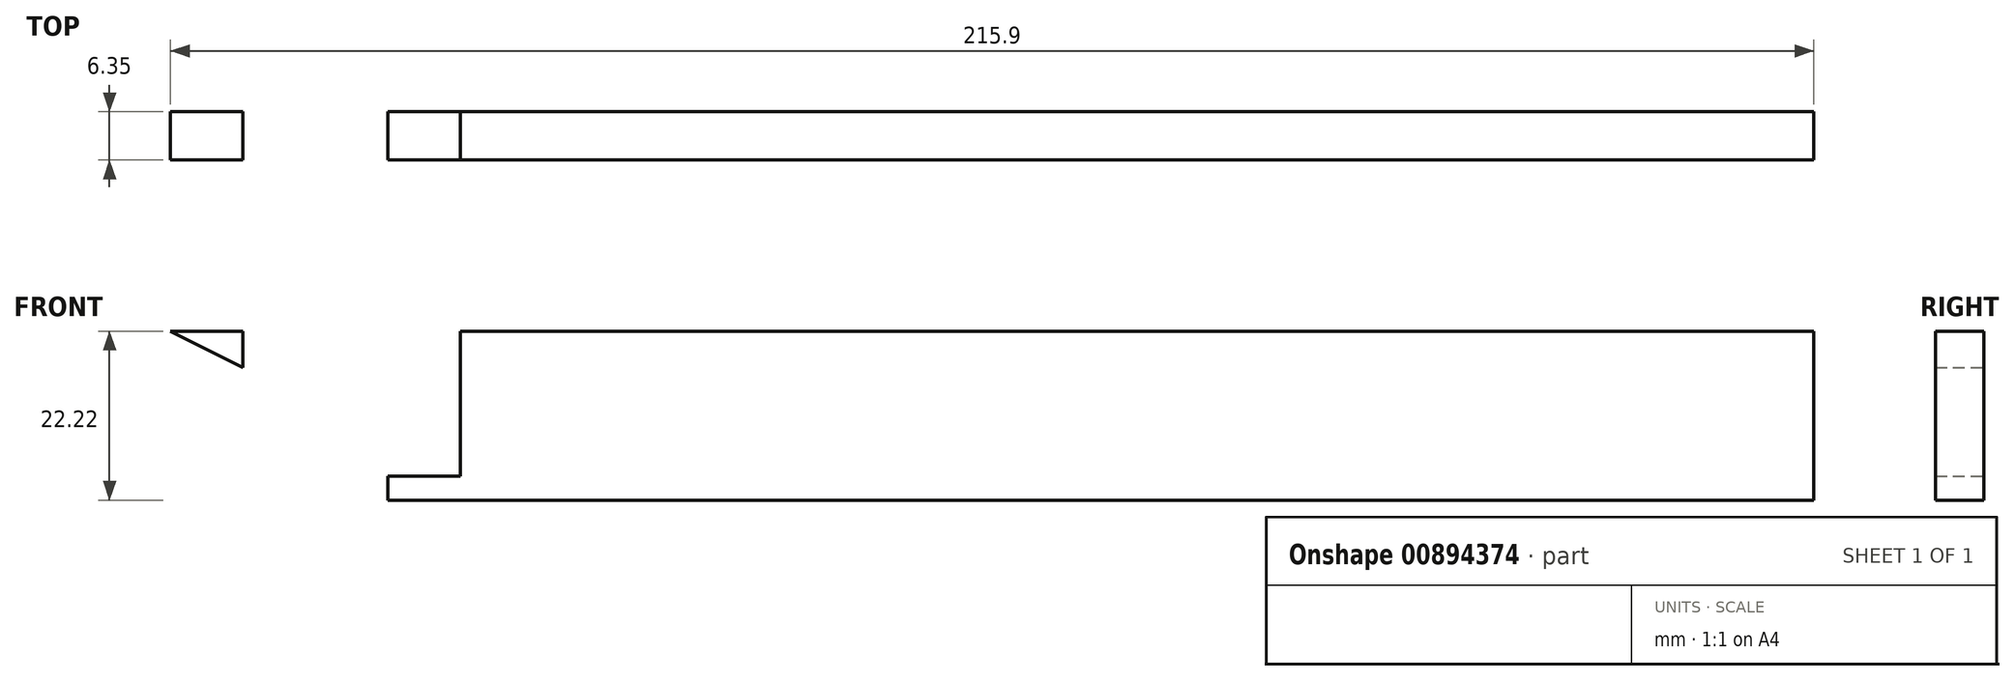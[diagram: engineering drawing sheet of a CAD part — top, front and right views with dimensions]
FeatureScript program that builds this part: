
annotation { "Feature Type Name" : "Feature", "Feature Type Description" : "" }
export const myFeature = defineFeature(function(context is Context, id is Id, definition is map)
    precondition{}
    {
        {
            var Q0;
            Q0=qCreatedBy(makeId("Front.planeOp"),FACE);
            var sketch = newSketch(context, id + "F0", { "sketchPlane" : qUnion([Q0])});
            skLineSegment(sketch, "E0.bottom", {"start": v(15.1, 18.32) * mm, "end": v(192.9, 18.32) * mm});
            skLineSegment(sketch, "E0.top", {"start": v(15.1, 40.54) * mm, "end": v(192.9, 40.54) * mm});
            skLineSegment(sketch, "E0.left", {"start": v(15.1, 18.32) * mm, "end": v(15.1, 40.54) * mm});
            skLineSegment(sketch, "E0.right", {"start": v(192.9, 18.32) * mm, "end": v(192.9, 40.54) * mm});
            skLineSegment(sketch, "E1.bottom", {"start": v(15.1, 18.32) * mm, "end": v(-23, 18.32) * mm});
            skLineSegment(sketch, "E1.top", {"start": v(15.1, 40.54) * mm, "end": v(-23, 40.54) * mm});
            skLineSegment(sketch, "E2.left", {"start": v(-23, 18.32) * mm, "end": v(-23, 15.4) * mm});
            skLineSegment(sketch, "E2.right", {"start": v(-188.1, 18.32) * mm, "end": v(-188.1, -42.13) * mm});
            skArc(sketch, "E3", {"start": v(-23, 18.32) * mm, "mid": v(-36.7, 0.58) * mm, "end": v(-44.36, -20.47) * mm});
            skArc(sketch, "E4", {"start": v(-70.9, 0.58) * mm, "mid": v(-60.95, -14.13) * mm, "end": v(-44.36, -20.47) * mm});
            skPoint(sketch, "E4.startSnap0", {"position": v(-36.7, 0.58) * mm});
            skArc(sketch, "E5", {"start": v(-23, 40.54) * mm, "mid": v(-33.87, 38.07) * mm, "end": v(-42.6, 31.15) * mm});
            skArc(sketch, "E6", {"start": v(-188.1, -42.13) * mm, "mid": v(-127.75, -25.58) * mm, "end": v(-70.9, 0.58) * mm});
            skArc(sketch, "E7", {"start": v(-129.8, 24.44) * mm, "mid": v(-159.01, 21.95) * mm, "end": v(-188.1, 18.32) * mm});
            skArc(sketch, "E8.0", {"start": v(-83.69, 13.36) * mm, "mid": v(-129.64, 11.73) * mm, "end": v(-175.4, 7.24) * mm});
            skArc(sketch, "E8.1", {"start": v(-82.7, 8.57) * mm, "mid": v(-83.01, 11) * mm, "end": v(-83.69, 13.36) * mm});
            skArc(sketch, "E8.2", {"start": v(-175.4, -26.5) * mm, "mid": v(-127.88, -12.07) * mm, "end": v(-82.7, 8.57) * mm});
            skLineSegment(sketch, "E8.3", {"start": v(-175.4, 7.24) * mm, "end": v(-175.4, -26.5) * mm});
            skPoint(sketch, "E9", {"position": v(5.57, 21.5) * mm});
            skLineSegment(sketch, "E10", {"start": v(5.57, 21.5) * mm, "end": v(5.57, 18.32) * mm});
            skLineSegment(sketch, "E11", {"start": v(5.57, 21.5) * mm, "end": v(15.1, 21.5) * mm});
            skLineSegment(sketch, "E12", {"start": v(-23, 40.54) * mm, "end": v(-14.68, 40.54) * mm});
            skLineSegment(sketch, "E13", {"start": v(-23, 40.54) * mm, "end": v(-13.48, 40.54) * mm});
            skLineSegment(sketch, "E14", {"start": v(-13.48, 40.54) * mm, "end": v(-13.48, 35.78) * mm});
            skLineSegment(sketch, "E15", {"start": v(-13.48, 35.78) * mm, "end": v(-23, 40.54) * mm});
            skFitSpline(sketch, "E16", {"points": [v(-42.6, 31.15) * mm, v(-56.97, 17.81) * mm, v(-88.1, 26.02) * mm], "startDerivative": vector(-27.78, -40.13) * mm, "endDerivative": vector(-61.83, 26.33) * mm});
            skFitSpline(sketch, "E17", {"points": [v(-72.62, 19.8) * mm, v(-98.6, 25.84) * mm, v(-129.8, 24.44) * mm], "startDerivative": vector(-52.72, 15.41) * mm, "endDerivative": vector(-61.46, -7.14) * mm});
            skSolve(sketch);
        }
        {
            var Q0;
            {var subQ3=sQuery(id+"F0.wireOp",EDGE,"E1.top");Q0=makeQuery(id+"F0.imprint","IMPRINT",FACE,{"disambiguationData":[TD([[makeQuery(id+"F0.imprint","IMPRINT",EDGE,{"derivedFrom":subQ3}),1.0]])]});}
            var Q1;
            {var subQ3=sQuery(id+"F0.wireOp",EDGE,"E10");Q1=makeQuery(id+"F0.imprint","IMPRINT",FACE,{"disambiguationData":[TD([[makeQuery(id+"F0.imprint","IMPRINT",EDGE,{"derivedFrom":subQ3}),1.0]])]});}
            var Q2;
            {var subQ1=sQuery(id+"F0.wireOp",EDGE,"E0.bottom");Q2=makeQuery(id+"F0.imprint","IMPRINT",FACE,{"disambiguationData":[TD([[makeQuery(id+"F0.imprint","IMPRINT",EDGE,{"derivedFrom":subQ1}),1.0]])]});}
            extrude(context, id + "F1", {"entities" : qUnion([Q0, Q1, Q2]), "depth" : 6.35 * mm, "offsetDistance" : 25.4 * mm});
        }
    });
